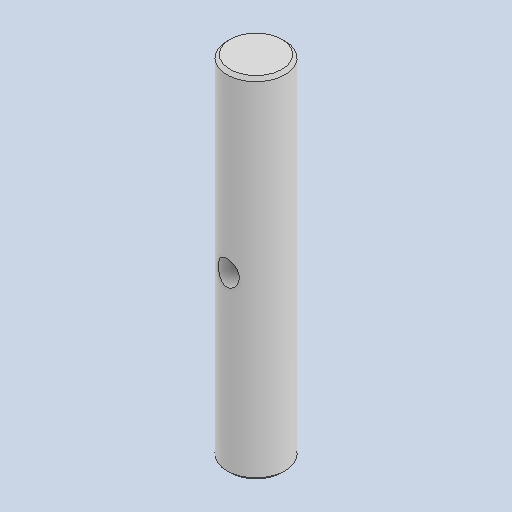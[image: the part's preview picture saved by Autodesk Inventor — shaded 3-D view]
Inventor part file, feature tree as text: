
AUTODESK INVENTOR PART (.ipt)
format: ipt  version: 2022 (Build 260153000, 153)  size: 79,872 bytes
history: native  units: in
note: dims shown in document units (in); Inventor stores cm internally (conversion verified against a paired STEP export)
features: chamfer x1
ambient origin geometry x8: Origin, YZ Plane, XZ Plane, XY Plane, X Axis, Y Axis, Z Axis, Center Point
bodies: Solid1 (feature_tree)
feature tree (1):
  chamfer  "Chamfer1"  [1 undecoded]
note: 1 required parameter value undecoded (feature->parameter linkage not recoverable at this tier; creation-order binding heuristic only, values carry confidence <= 0.55)
